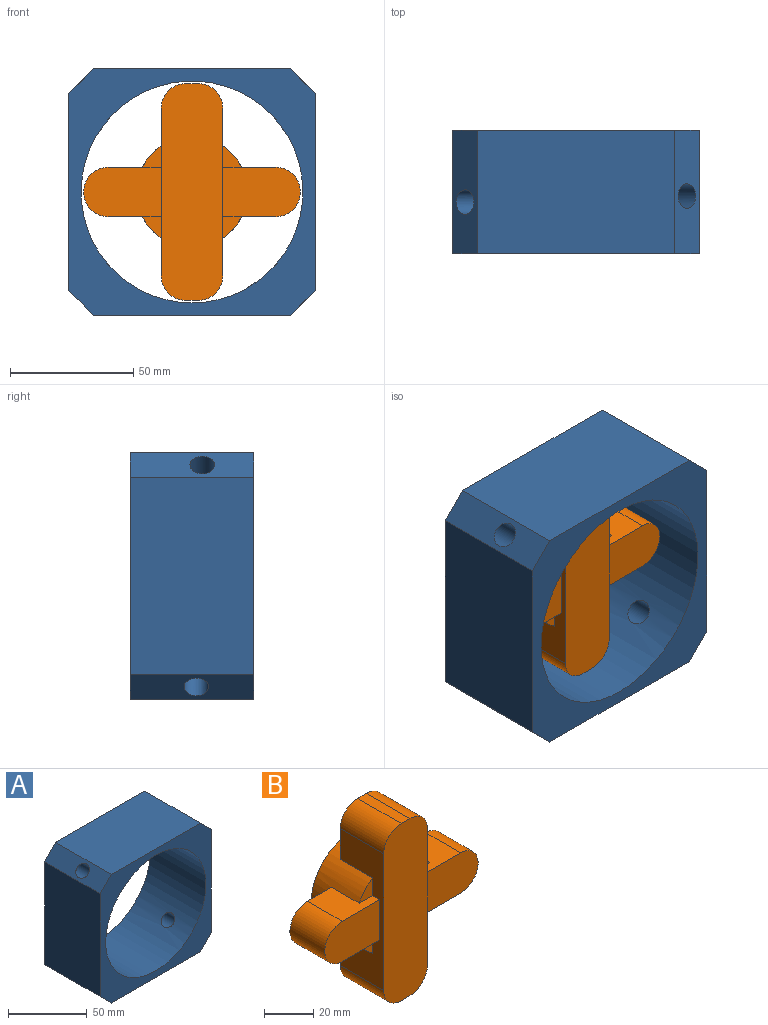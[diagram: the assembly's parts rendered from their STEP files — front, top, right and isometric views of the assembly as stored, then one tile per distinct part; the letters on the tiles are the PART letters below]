
ASSEMBLY  parts=2 mates=1
PART A: 15 faces, bbox 100x50x100 mm
  f0: cylinder r=45mm len=90mm, axis (0,1,0), area 13822.4mm2, adj f5,f6,f8,f9,f13,f14
  f1: plane 80x50mm, normal (1,0,0), area 4000mm2, adj f5,f6,f7,f12
  f2: plane 80x50mm, normal (0,0,1), area 4000mm2, adj f5,f6,f7,f11
  f3: plane 80x50mm, normal (-1,0,0), area 4000mm2, adj f5,f6,f10,f11
  f4: plane 80x50mm, normal (0,0,-1), area 4000mm2, adj f5,f6,f10,f12
  f5: plane 100x100mm, normal (0,-1,0), area 3438.3mm2, adj f0,f1,f2,f3,f4,f7,f10,f11
  f6: plane 100x100mm, normal (0,1,0), area 3438.3mm2, adj f0,f1,f2,f3,f4,f7,f10,f11
  f7: plane 50x10mm, normal (0.71,0,0.71), area 628.6mm2, adj f1,f2,f5,f6,f8
  f8: cylinder r=5mm len=20.45mm, axis (0.71,0,0.71), area 589.9mm2, adj f0,f7
  f9: cylinder r=5mm len=20.45mm, axis (0.71,0,0.71), area 590mm2, adj f0,f10
  f10: plane 50x10mm, normal (-0.71,0,-0.71), area 628.6mm2, adj f3,f4,f5,f6,f9
  f11: plane 50x10mm, normal (-0.71,0,0.71), area 628.6mm2, adj f2,f3,f5,f6,f14
  f12: plane 50x10mm, normal (0.71,0,-0.71), area 628.6mm2, adj f1,f4,f5,f6,f13
  f13: cylinder r=5mm len=20.45mm, axis (0.71,0,-0.71), area 589.9mm2, adj f0,f12
  f14: cylinder r=5mm len=20.45mm, axis (0.71,0,-0.71), area 590mm2, adj f0,f11
PART B: 29 faces, bbox 88x31.5x88 mm
  f0: plane 25.29x25mm, normal (0,1,0), area 525mm2, adj f1,f2,f5,f13,f23,f24
  f1: plane 68x25mm, normal (1,0,0), area 925.9mm2, adj f0,f3,f4,f13,f14,f15,f17,f19
  f2: plane 68x25mm, normal (-1,0,0), area 925.9mm2, adj f0,f3,f4,f7,f9,f10,f11,f12
  f3: plane 25.29x25mm, normal (0,1,0), area 525mm2, adj f1,f2,f6,f13,f26,f27
  f4: plane 88x25mm, normal (0,-1,0), area 2114.2mm2, adj f1,f2,f5,f6,f23,f24,f26,f27
  f5: plane 25x5mm, normal (0,0,1), area 125mm2, adj f0,f4,f23,f24
  f6: plane 25x5mm, normal (0,0,-1), area 125mm2, adj f3,f4,f26,f27
  f7: plane 8.71x7.66mm, normal (0,-1,0), area 39.2mm2, adj f2,f12,f13
  f8: cylinder r=5mm len=10mm, axis (0,1,0), area 204.6mm2, adj f16,f22
  f9: plane 8.71x7.66mm, normal (0,-1,0), area 39.2mm2, adj f2,f11,f13
  f10: plane 31.5x20mm, normal (0,-1,0), area 587.1mm2, adj f2,f11,f12,f28
  f11: plane 21.5x20mm, normal (0,0,-1), area 308.4mm2, adj f2,f9,f10,f13,f18,f28
  f12: plane 21.5x20mm, normal (0,0,1), area 308.4mm2, adj f2,f7,f10,f13,f18,f28
  f13: cylinder r=22.5mm len=45mm, axis (0,1,0), area 1896.1mm2, adj f0,f1,f2,f3,f7,f9,f11,f12
  f14: plane 8.71x7.66mm, normal (0,-1,0), area 39.2mm2, adj f1,f13,f20
  f15: plane 8.71x7.66mm, normal (0,-1,0), area 39.2mm2, adj f1,f13,f19
  f16: plane 45x45mm, normal (0,1,0), area 1511.9mm2, adj f8,f13
  f17: plane 31.5x20mm, normal (0,-1,0), area 587.1mm2, adj f1,f19,f20,f25
  f18: plane 23.84x20mm, normal (0,1,0), area 402.4mm2, adj f11,f12,f13,f28
  f19: plane 21.5x20mm, normal (0,0,-1), area 308.4mm2, adj f1,f13,f15,f17,f21,f25
  f20: plane 21.5x20mm, normal (0,0,1), area 308.4mm2, adj f1,f13,f14,f17,f21,f25
  f21: plane 23.84x20mm, normal (0,1,0), area 402.4mm2, adj f13,f19,f20,f25
  f22: plane 10x10mm, normal (0,1,0), area 78.5mm2, adj f8
  f23: cylinder r=10mm len=25mm, axis (0,-1,0), area 392.7mm2, adj f0,f1,f4,f5
  f24: cylinder r=10mm len=25mm, axis (0,1,0), area 392.7mm2, adj f0,f2,f4,f5
  f25: cylinder r=10mm len=20mm, axis (0,1,0), area 628.3mm2, adj f17,f19,f20,f21
  f26: cylinder r=10mm len=25mm, axis (0,1,0), area 392.7mm2, adj f1,f3,f4,f6
  f27: cylinder r=10mm len=25mm, axis (0,-1,0), area 392.7mm2, adj f2,f3,f4,f6
  f28: cylinder r=10mm len=20mm, axis (0,1,0), area 628.3mm2, adj f10,f11,f12,f18
PLACE A t=(103.3,50,68.74)mm
PLACE B t=(103.3,50,68.74)mm
MATE planar B.f13 <-> A.f0  axis (0,1,0) through (103.3,50,68.74)mm
